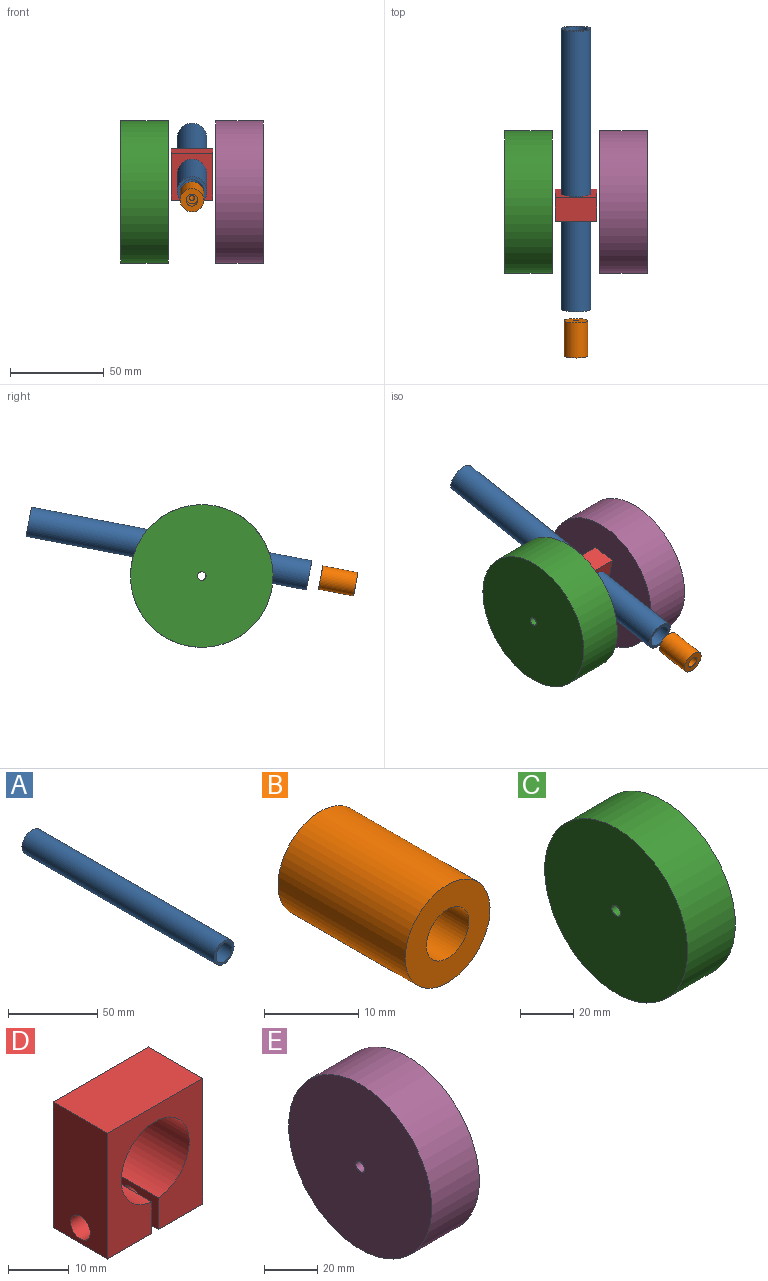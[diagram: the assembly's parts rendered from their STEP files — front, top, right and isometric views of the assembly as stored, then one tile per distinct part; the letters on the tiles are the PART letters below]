
ASSEMBLY  parts=5 mates=4
PART A: 4 faces, bbox 15.9x152.4x15.9 mm
  f0: cylinder r=6.35mm len=152.4mm, axis (0,1,0), area 6080.5mm2, adj f2,f3
  f1: cylinder r=7.94mm len=152.4mm, axis (0,1,0), area 7600.6mm2, adj f2,f3
  f2: plane 15.88x15.88mm, normal (0,-1,0), area 71.3mm2, adj f0,f1
  f3: plane 15.88x15.88mm, normal (0,1,0), area 71.3mm2, adj f0,f1
PART B: 6 faces, bbox 12.7x19.1x12.7 mm
  f0: cylinder r=6.35mm len=19.05mm, axis (0,1,0), area 760.1mm2, adj f1,f2
  f1: plane 12.7x12.7mm, normal (0,-1,0), area 95mm2, adj f0,f3
  f2: plane 12.7x12.7mm, normal (0,1,0), area 120mm2, adj f0,f5
  f3: cylinder r=3.17mm len=6.35mm, axis (0,-1,0), area 126.7mm2, adj f1,f4
  f4: plane 6.35x6.35mm, normal (0,-1,0), area 25mm2, adj f3,f5
  f5: cylinder r=1.46mm len=12.7mm, axis (0,1,0), area 116.5mm2, adj f2,f4
PART C: 4 faces, bbox 25.4x76.2x76.2 mm
  f0: cylinder r=38.1mm len=76.2mm, axis (1,0,0), area 6080.5mm2, adj f2,f3
  f1: cylinder r=2.29mm len=25.4mm, axis (1,0,0), area 364.8mm2, adj f2,f3
  f2: plane 76.2x76.2mm, normal (-1,0,0), area 4543.9mm2, adj f0,f1
  f3: plane 76.2x76.2mm, normal (1,0,0), area 4543.9mm2, adj f0,f1
PART D: 12 faces, bbox 22.2x12.7x25.4 mm
  f0: cylinder r=7.94mm len=15.88mm, axis (0,1,0), area 613.4mm2, adj f1,f7,f8,f9
  f1: plane 12.7x6.39mm, normal (-1,0,0), area 64.7mm2, adj f0,f2,f8,f9,f11
  f2: plane 12.7x10.33mm, normal (0,0,-1), area 131.1mm2, adj f1,f3,f8,f9
  f3: plane 25.4x12.7mm, normal (1,0,0), area 306.2mm2, adj f2,f4,f8,f9,f11
  f4: plane 22.23x12.7mm, normal (0,0,1), area 282.3mm2, adj f3,f5,f8,f9
  f5: plane 25.4x12.7mm, normal (-1,0,0), area 306.2mm2, adj f4,f6,f8,f9,f10
  f6: plane 12.7x10.33mm, normal (0,0,-1), area 131.1mm2, adj f5,f7,f8,f9
  f7: plane 12.7x6.39mm, normal (1,0,0), area 64.7mm2, adj f0,f6,f8,f9,f10
  f8: plane 25.4x22.23mm, normal (0,-1,0), area 356.6mm2, adj f0,f1,f2,f3,f4,f5,f6,f7
  f9: plane 25.4x22.23mm, normal (0,1,0), area 356.6mm2, adj f0,f1,f2,f3,f4,f5,f6,f7
  f10: cylinder r=2.29mm len=10.33mm, axis (1,0,0), area 148.3mm2, adj f5,f7
  f11: cylinder r=2.29mm len=10.33mm, axis (1,0,0), area 148.3mm2, adj f1,f3
PART E: 4 faces, bbox 25.4x76.2x76.2 mm
  f0: cylinder r=38.1mm len=76.2mm, axis (-1,0,0), area 6080.5mm2, adj f2,f3
  f1: cylinder r=2.29mm len=25.4mm, axis (-1,0,0), area 364.8mm2, adj f2,f3
  f2: plane 76.2x76.2mm, normal (1,0,0), area 4543.9mm2, adj f0,f1
  f3: plane 76.2x76.2mm, normal (-1,0,0), area 4543.9mm2, adj f0,f1
PLACE A rot(axis=(0.08,-0.99,-0.09),100deg) t=(0.36,73.8,18.09)mm
PLACE B rot(axis=(0.08,-0.99,-0.09),100deg) t=(0.36,-82.13,-11.7)mm
PLACE C rot(axis=(1,0,0),10.8deg) t=(-1.22,-14.43,1.24)mm
PLACE D rot(axis=(1,0,0),10.8deg) t=(0.36,-14.43,1.24)mm fixed
PLACE E rot(axis=(1,0,0),10.8deg) t=(1.93,-14.43,1.24)mm
MATE slider B.f3 <-> A.f0  axis (0,-0.98,-0.19) through (0.36,-100.84,-15.27)mm
MATE revolute E.f0 <-> D.f10  axis (-1,0,0) through (13.04,-18.58,-10.87)mm
MATE revolute C.f0 <-> D.f10  axis (1,0,0) through (-12.33,-18.58,-10.87)mm
MATE cylindrical A.f1 <-> D.f0  axis (0,0.98,0.19) through (0.36,73.8,18.09)mm
